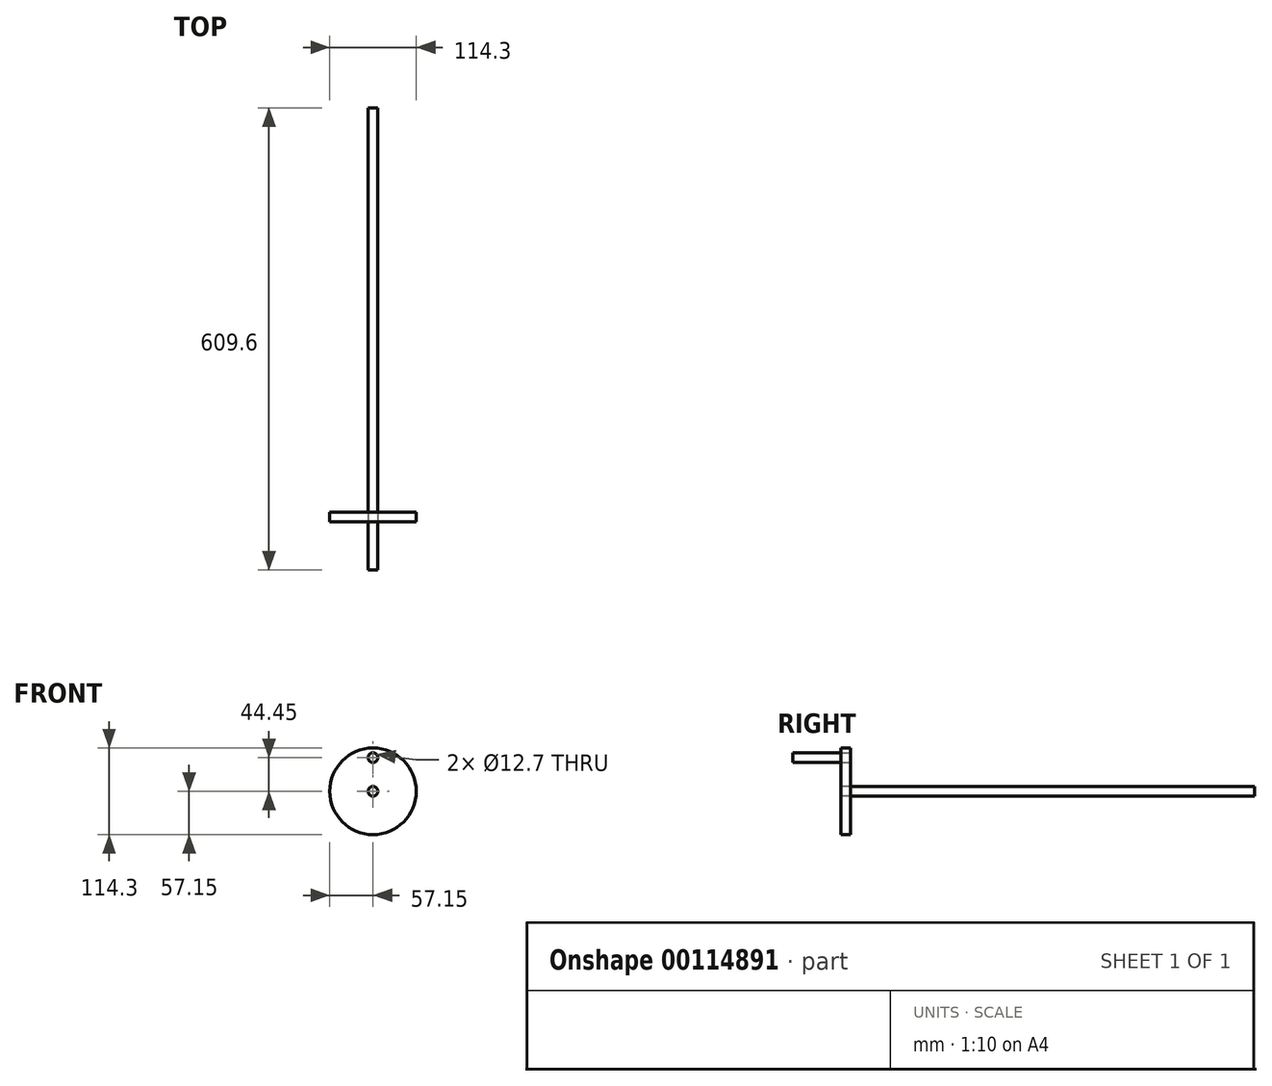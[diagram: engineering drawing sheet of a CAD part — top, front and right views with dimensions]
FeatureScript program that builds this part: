
annotation { "Feature Type Name" : "Feature", "Feature Type Description" : "" }
export const myFeature = defineFeature(function(context is Context, id is Id, definition is map)
    precondition{}
    {
        {
            var Q0;
            Q0=qCreatedBy(makeId("Front.planeOp"),FACE);
            var sketch = newSketch(context, id + "F0", { "sketchPlane" : qUnion([Q0])});
            skCircle(sketch, "E0", {"center": v(0, 0) * mm, "radius": 57.15 * mm});
            skSolve(sketch);
        }
        {
            var Q0;
            Q0 = qSketchRegion(id + "F0", true);
            extrude(context, id + "F1", {"entities" : qUnion([Q0]), "depth" : 12.7 * mm});
        }
        {
            var Q0;
            Q0=makeQuery(id+"F1.opExtrude","CAP_FACE",FACE,{"disambiguationData":[OSD([sQuery(id+"F0.wireOp",EDGE,"E0")])],"isStart":false});
            var sketch = newSketch(context, id + "F2", { "sketchPlane" : qUnion([Q0])});
            skCircle(sketch, "E1", {"center": v(0, 0) * mm, "radius": 6.35 * mm});
            skSolve(sketch);
        }
        {
            var Q0;
            Q0 = qSketchRegion(id + "F2", true);
            extrude(context, id + "F3", {"entities" : qUnion([Q0]), "operationType" : NewBodyOperationType.REMOVE, "endBound" : BoundingType.THROUGH_ALL, "oppositeDirection" : true, "depth" : 25.4 * mm});
        }
        {
            var Q0;
            Q0=makeQuery(id+"F1.opExtrude","CAP_FACE",FACE,{"disambiguationData":[OSD([sQuery(id+"F0.wireOp",EDGE,"E0")])],"isStart":false});
            var sketch = newSketch(context, id + "F4", { "sketchPlane" : qUnion([Q0])});
            skCircle(sketch, "E2", {"center": v(0, 0) * mm, "radius": 6.35 * mm});
            skSolve(sketch);
        }
        {
            var Q0;
            Q0 = qSketchRegion(id + "F4", true);
            var Q1;
            Q1=sQuery(id+"F4.wireOp",EDGE,"E2");
            extrude(context, id + "F5", {"entities" : qUnion([Q0]), "surfaceEntities" : qUnion([Q1]), "oppositeDirection" : true, "depth" : 546.1 * mm});
        }
        {
            var Q0;
            Q0=makeQuery(id+"F1.opExtrude","CAP_FACE",FACE,{"disambiguationData":[OSD([sQuery(id+"F0.wireOp",EDGE,"E0")])],"isStart":true});
            var sketch = newSketch(context, id + "F6", { "sketchPlane" : qUnion([Q0])});
            skCircle(sketch, "E3", {"center": v(0, 44.45) * mm, "radius": 6.35 * mm});
            skLineSegment(sketch, "E4", {"start": v(0, 0) * mm, "end": v(0, 44.45) * mm, "construction": true});
            skSolve(sketch);
        }
        {
            var Q0;
            Q0 = qSketchRegion(id + "F6", true);
            extrude(context, id + "F7", {"entities" : qUnion([Q0]), "operationType" : NewBodyOperationType.REMOVE, "endBound" : BoundingType.THROUGH_ALL, "oppositeDirection" : true, "depth" : 25.4 * mm});
        }
        {
            var Q0;
            Q0=makeQuery(id+"F6.imprint","IMPRINT",FACE,{"disambiguationData":[TD([[makeQuery(id+"F6.imprint","IMPRINT",EDGE,{"derivedFrom":sQuery(id+"F6.wireOp",EDGE,"E3")}),1.0]])]});
            var Q1;
            Q1=sQuery(id+"F6.wireOp",EDGE,"E3");
            extrude(context, id + "F8", {"entities" : qUnion([Q0]), "surfaceEntities" : qUnion([Q1]), "oppositeDirection" : true, "depth" : 76.2 * mm});
        }
    });
